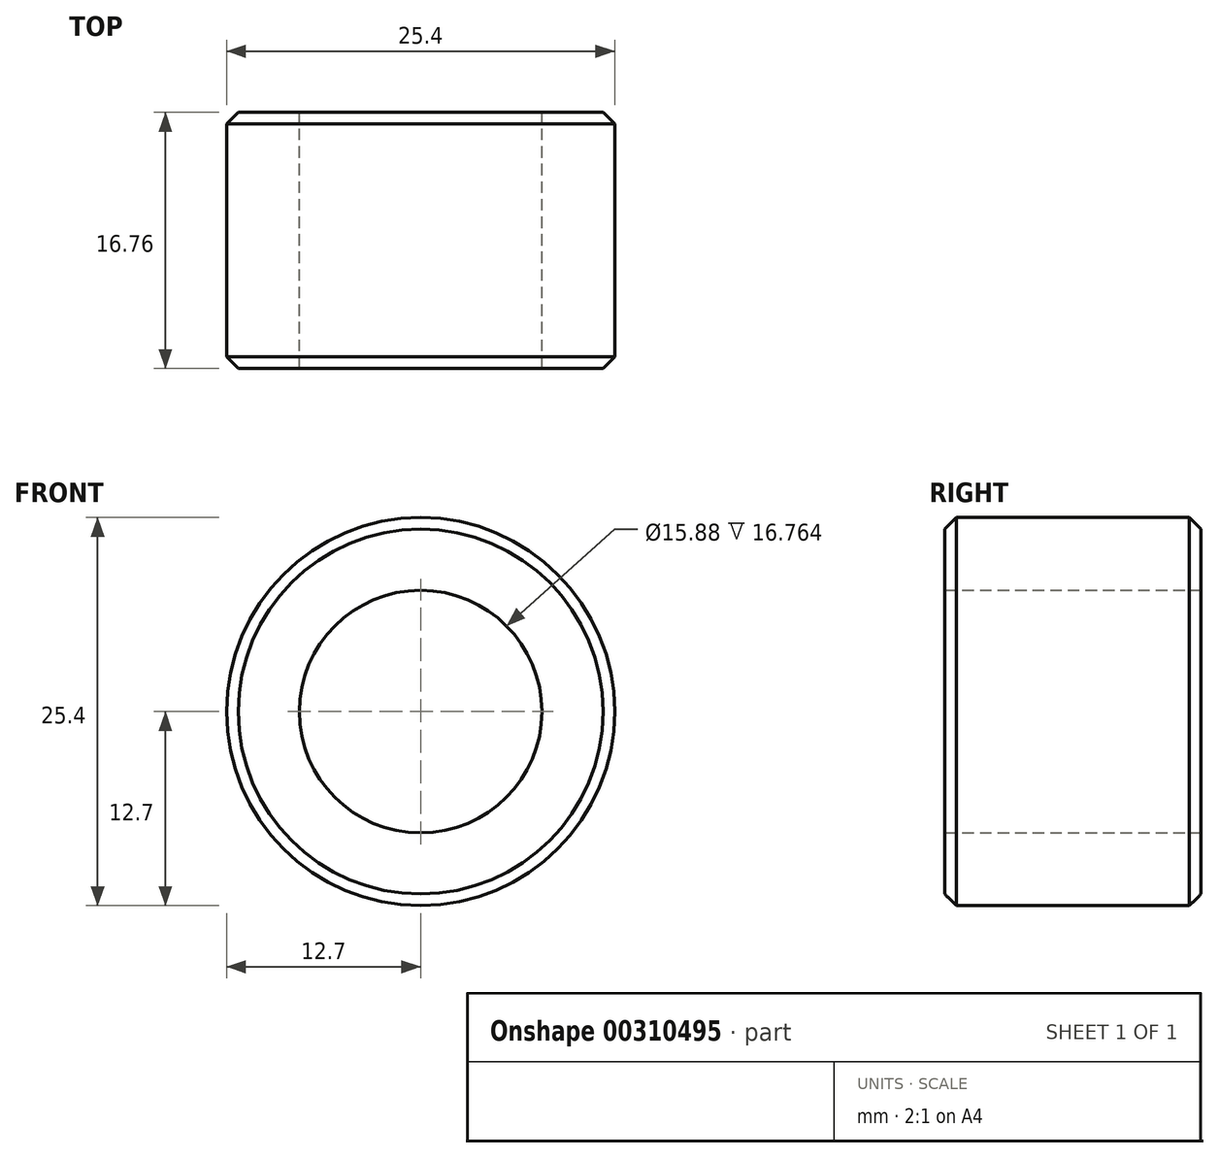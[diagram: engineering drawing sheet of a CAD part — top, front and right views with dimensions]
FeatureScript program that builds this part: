
annotation { "Feature Type Name" : "Feature", "Feature Type Description" : "" }
export const myFeature = defineFeature(function(context is Context, id is Id, definition is map)
    precondition{}
    {
        {
            var Q0;
            Q0=qCreatedBy(makeId("Front.planeOp"),FACE);
            var sketch = newSketch(context, id + "F0", { "sketchPlane" : qUnion([Q0])});
            skCircle(sketch, "E0", {"center": v(0, 0) * mm, "radius": 12.7 * mm});
            skCircle(sketch, "E1", {"center": v(0, 0) * mm, "radius": 7.94 * mm});
            skSolve(sketch);
        }
        {
            var Q0;
            Q0=qSketchRegion(id+"F0",true);
            extrude(context, id + "F1", {"entities" : qUnion([Q0]), "endBound" : BoundingType.SYMMETRIC, "depth" : 16.76 * mm});
        }
        {
            var Q0;
            Q0=makeQuery(id+"F1.opExtrude","CAP_EDGE",EDGE,{"disambiguationData":[OSD([sQuery(id+"F0.wireOp",EDGE,"E0")])],"isStart":false});
            var Q1;
            Q1=makeQuery(id+"F1.opExtrude","CAP_EDGE",EDGE,{"disambiguationData":[OSD([sQuery(id+"F0.wireOp",EDGE,"E0")])],"isStart":true});
            chamfer(context, id + "F2", {"entities" : qUnion([Q0, Q1]), "width" : 0.76 * mm, "tangentPropagation" : true});
        }
    });
